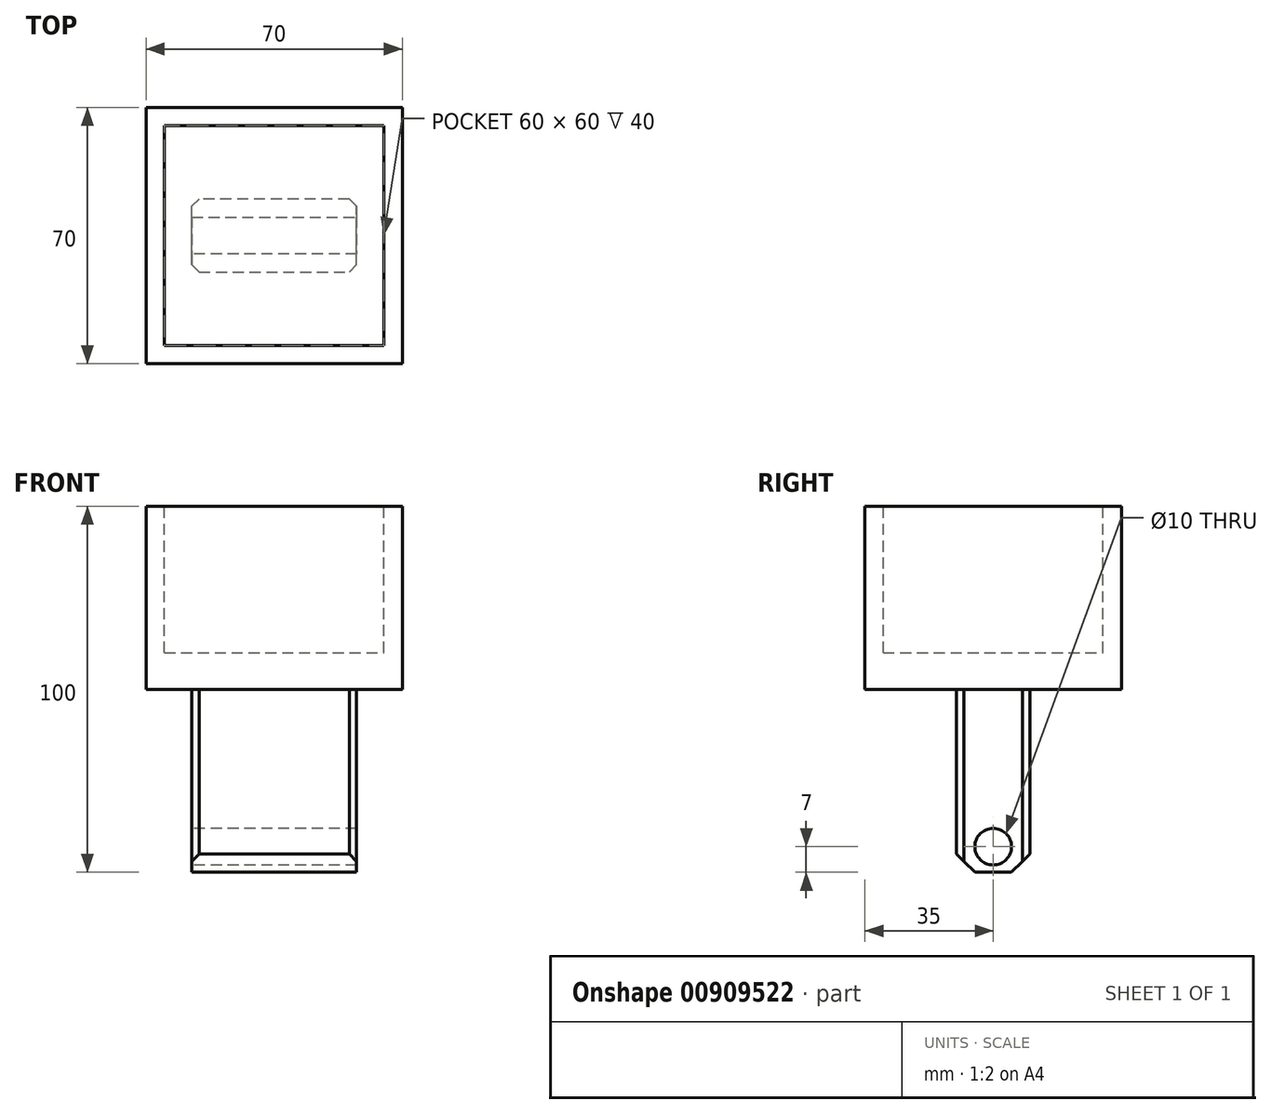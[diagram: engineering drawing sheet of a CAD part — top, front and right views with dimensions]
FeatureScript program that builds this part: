
annotation { "Feature Type Name" : "Feature", "Feature Type Description" : "" }
export const myFeature = defineFeature(function(context is Context, id is Id, definition is map)
    precondition{}
    {
        {
            var Q0;
            Q0=qCreatedBy(makeId("Top.planeOp"),FACE);
            var sketch = newSketch(context, id + "F0", { "sketchPlane" : qUnion([Q0])});
            skLineSegment(sketch, "E0.bottom", {"start": v(22.5, -10) * mm, "end": v(-22.5, -10) * mm});
            skLineSegment(sketch, "E0.top", {"start": v(22.5, 10) * mm, "end": v(-22.5, 10) * mm});
            skLineSegment(sketch, "E0.left", {"start": v(22.5, -10) * mm, "end": v(22.5, 10) * mm});
            skLineSegment(sketch, "E0.right", {"start": v(-22.5, -10) * mm, "end": v(-22.5, 10) * mm});
            skPoint(sketch, "E0.middle", {"position": v(0, 0) * mm});
            skSolve(sketch);
        }
        {
            var Q0;
            Q0 = qSketchRegion(id + "F0", true);
            extrude(context, id + "F1", {"entities" : qUnion([Q0]), "depth" : 50 * mm, "offsetDistance" : 25 * mm});
        }
        {
            var Q0;
            Q0=makeQuery(id+"F1.opExtrude","SWEPT_FACE",FACE,{"disambiguationData":[OSD([sQuery(id+"F0.wireOp",EDGE,"E0.right")])]});
            var sketch = newSketch(context, id + "F2", { "sketchPlane" : qUnion([Q0])});
            skCircle(sketch, "E1", {"center": v(0, 7) * mm, "radius": 5 * mm});
            skSolve(sketch);
        }
        {
            var Q0;
            Q0=makeQuery(id+"F1.opExtrude","SWEPT_EDGE",EDGE,{"disambiguationData":[OSD([sQuery(id+"F0.wireOp",EDGE,"E0.bottom"),sQuery(id+"F0.wireOp",EDGE,"E0.right")])]});
            var Q1;
            Q1=makeQuery(id+"F1.opExtrude","SWEPT_EDGE",EDGE,{"disambiguationData":[OSD([sQuery(id+"F0.wireOp",EDGE,"E0.top"),sQuery(id+"F0.wireOp",EDGE,"E0.right")])]});
            var Q2;
            Q2=makeQuery(id+"F1.opExtrude","SWEPT_EDGE",EDGE,{"disambiguationData":[OSD([sQuery(id+"F0.wireOp",EDGE,"E0.bottom"),sQuery(id+"F0.wireOp",EDGE,"E0.left")])]});
            var Q3;
            Q3=makeQuery(id+"F1.opExtrude","SWEPT_EDGE",EDGE,{"disambiguationData":[OSD([sQuery(id+"F0.wireOp",EDGE,"E0.top"),sQuery(id+"F0.wireOp",EDGE,"E0.left")])]});
            chamfer(context, id + "F3", {"entities" : qUnion([Q0, Q1, Q2, Q3]), "width" : 2 * mm, "tangentPropagation" : true});
        }
        {
            var Q0;
            Q0=makeQuery(id+"F1.opExtrude","CAP_EDGE",EDGE,{"disambiguationData":[OSD([sQuery(id+"F0.wireOp",EDGE,"E0.top")])],"isStart":true});
            var Q1;
            Q1=makeQuery(id+"F1.opExtrude","CAP_EDGE",EDGE,{"disambiguationData":[OSD([sQuery(id+"F0.wireOp",EDGE,"E0.bottom")])],"isStart":true});
            chamfer(context, id + "F4", {"entities" : qUnion([Q0, Q1]), "width" : 5 * mm, "tangentPropagation" : true});
        }
        {
            var Q0;
            Q0=makeQuery(id+"F2.imprint","IMPRINT",FACE,{"disambiguationData":[TD([[makeQuery(id+"F2.imprint","IMPRINT",EDGE,{"derivedFrom":sQuery(id+"F2.wireOp",EDGE,"E1")}),1.0]])]});
            extrude(context, id + "F5", {"entities" : qUnion([Q0]), "operationType" : NewBodyOperationType.REMOVE, "endBound" : BoundingType.UP_TO_NEXT, "oppositeDirection" : true, "depth" : 25 * mm, "offsetDistance" : 25 * mm});
        }
        {
            var Q0;
            Q0=makeQuery(id+"F1.opExtrude","CAP_FACE",FACE,{"disambiguationData":[OSD([sQuery(id+"F0.wireOp",EDGE,"E0.bottom"),sQuery(id+"F0.wireOp",EDGE,"E0.top"),sQuery(id+"F0.wireOp",EDGE,"E0.left"),sQuery(id+"F0.wireOp",EDGE,"E0.right")])],"isStart":false});
            var sketch = newSketch(context, id + "F6", { "sketchPlane" : qUnion([Q0])});
            skLineSegment(sketch, "E2.bottom", {"start": v(-35, 35) * mm, "end": v(35, 35) * mm});
            skLineSegment(sketch, "E2.top", {"start": v(-35, -35) * mm, "end": v(35, -35) * mm});
            skLineSegment(sketch, "E2.left", {"start": v(-35, 35) * mm, "end": v(-35, -35) * mm});
            skLineSegment(sketch, "E2.right", {"start": v(35, 35) * mm, "end": v(35, -35) * mm});
            skPoint(sketch, "E2.middle", {"position": v(0, 0) * mm});
            skSolve(sketch);
        }
        {
            var Q0;
            Q0 = qSketchRegion(id + "F6", true);
            extrude(context, id + "F7", {"entities" : qUnion([Q0]), "operationType" : NewBodyOperationType.ADD, "depth" : 50 * mm, "offsetDistance" : 25 * mm});
        }
        {
            var Q0;
            Q0=makeQuery(id+"F7.opExtrude","CAP_FACE",FACE,{"disambiguationData":[OSD([sQuery(id+"F6.wireOp",EDGE,"E2.bottom"),sQuery(id+"F6.wireOp",EDGE,"E2.top"),sQuery(id+"F6.wireOp",EDGE,"E2.left"),sQuery(id+"F6.wireOp",EDGE,"E2.right")])],"isStart":false});
            var sketch = newSketch(context, id + "F8", { "sketchPlane" : qUnion([Q0])});
            skLineSegment(sketch, "E3.bottom", {"start": v(-30, -30) * mm, "end": v(30, -30) * mm});
            skLineSegment(sketch, "E3.top", {"start": v(-30, 30) * mm, "end": v(30, 30) * mm});
            skLineSegment(sketch, "E3.left", {"start": v(-30, -30) * mm, "end": v(-30, 30) * mm});
            skLineSegment(sketch, "E3.right", {"start": v(30, -30) * mm, "end": v(30, 30) * mm});
            skPoint(sketch, "E3.middle", {"position": v(0, 0) * mm});
            skSolve(sketch);
        }
        {
            var Q0;
            Q0=makeQuery(id+"F8.imprint","IMPRINT",FACE,{"disambiguationData":[TD([[makeQuery(id+"F8.imprint","IMPRINT",EDGE,{"derivedFrom":sQuery(id+"F8.wireOp",EDGE,"E3.bottom")}),1.0]])]});
            extrude(context, id + "F9", {"entities" : qUnion([Q0]), "operationType" : NewBodyOperationType.REMOVE, "oppositeDirection" : true, "depth" : 40 * mm, "offsetDistance" : 25 * mm});
        }
    });
